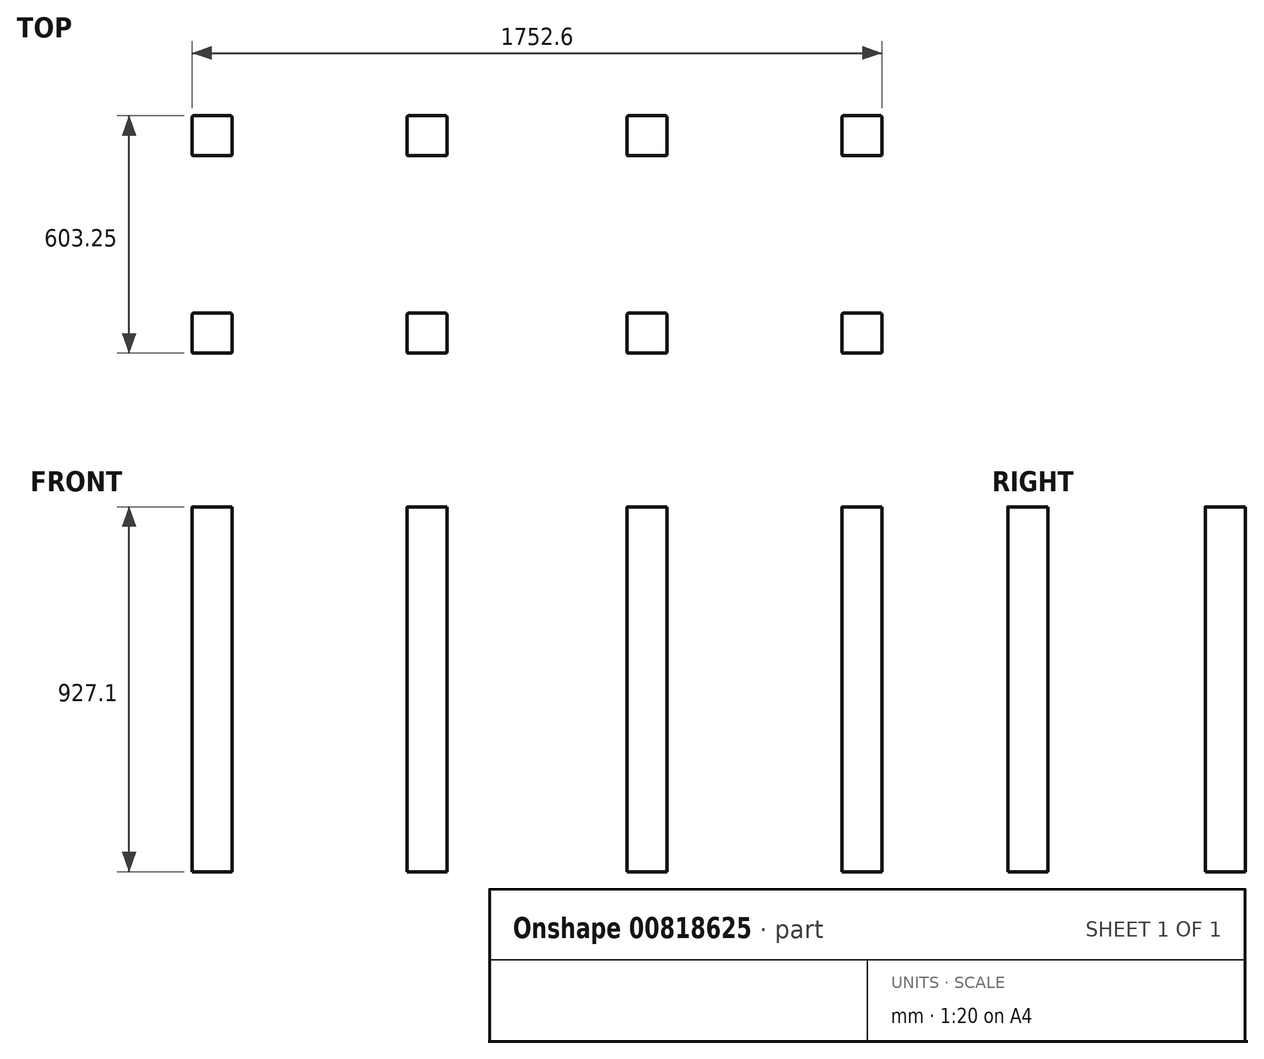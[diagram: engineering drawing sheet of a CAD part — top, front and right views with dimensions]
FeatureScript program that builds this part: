
annotation { "Feature Type Name" : "Feature", "Feature Type Description" : "" }
export const myFeature = defineFeature(function(context is Context, id is Id, definition is map)
    precondition{}
    {
        {
            var Q0;
            Q0=qCreatedBy(makeId("Top.planeOp"),FACE);
            var sketch = newSketch(context, id + "F0", { "sketchPlane" : qUnion([Q0])});
            skPoint(sketch, "E0.middle", {"position": v(0, 0) * mm});
            skLineSegment(sketch, "E1.bottom", {"start": v(-876.3, -285.75) * mm, "end": v(-774.7, -285.75) * mm});
            skLineSegment(sketch, "E1.top", {"start": v(-876.3, -184.15) * mm, "end": v(-774.7, -184.15) * mm});
            skLineSegment(sketch, "E1.left", {"start": v(-876.3, -285.75) * mm, "end": v(-876.3, -184.15) * mm});
            skLineSegment(sketch, "E1.right", {"start": v(-774.7, -285.75) * mm, "end": v(-774.7, -184.15) * mm});
            skLineSegment(sketch, "E2.bottom", {"start": v(-876.3, 317.5) * mm, "end": v(-774.7, 317.5) * mm});
            skLineSegment(sketch, "E2.top", {"start": v(-876.3, 215.9) * mm, "end": v(-774.7, 215.9) * mm});
            skLineSegment(sketch, "E2.left", {"start": v(-876.3, 317.5) * mm, "end": v(-876.3, 215.9) * mm});
            skLineSegment(sketch, "E2.right", {"start": v(-774.7, 317.5) * mm, "end": v(-774.7, 215.9) * mm});
            skLineSegment(sketch, "E3.bottom", {"start": v(876.3, -285.75) * mm, "end": v(774.7, -285.75) * mm});
            skLineSegment(sketch, "E3.top", {"start": v(876.3, -184.15) * mm, "end": v(774.7, -184.15) * mm});
            skLineSegment(sketch, "E3.left", {"start": v(876.3, -285.75) * mm, "end": v(876.3, -184.15) * mm});
            skLineSegment(sketch, "E3.right", {"start": v(774.7, -285.75) * mm, "end": v(774.7, -184.15) * mm});
            skLineSegment(sketch, "E4.bottom", {"start": v(876.3, 317.5) * mm, "end": v(774.7, 317.5) * mm});
            skLineSegment(sketch, "E4.top", {"start": v(876.3, 215.9) * mm, "end": v(774.7, 215.9) * mm});
            skLineSegment(sketch, "E4.left", {"start": v(876.3, 317.5) * mm, "end": v(876.3, 215.9) * mm});
            skLineSegment(sketch, "E4.right", {"start": v(774.7, 317.5) * mm, "end": v(774.7, 215.9) * mm});
            skLineSegment(sketch, "E5.bottom", {"start": v(-330.2, -285.75) * mm, "end": v(-228.6, -285.75) * mm});
            skLineSegment(sketch, "E5.top", {"start": v(-330.2, -184.15) * mm, "end": v(-228.6, -184.15) * mm});
            skLineSegment(sketch, "E5.left", {"start": v(-330.2, -285.75) * mm, "end": v(-330.2, -184.15) * mm});
            skLineSegment(sketch, "E5.right", {"start": v(-228.6, -285.75) * mm, "end": v(-228.6, -184.15) * mm});
            skLineSegment(sketch, "E6.bottom", {"start": v(330.2, -285.75) * mm, "end": v(228.6, -285.75) * mm});
            skLineSegment(sketch, "E6.top", {"start": v(330.2, -184.15) * mm, "end": v(228.6, -184.15) * mm});
            skLineSegment(sketch, "E6.left", {"start": v(330.2, -285.75) * mm, "end": v(330.2, -184.15) * mm});
            skLineSegment(sketch, "E6.right", {"start": v(228.6, -285.75) * mm, "end": v(228.6, -184.15) * mm});
            skLineSegment(sketch, "E7.bottom", {"start": v(330.2, 317.5) * mm, "end": v(228.6, 317.5) * mm});
            skLineSegment(sketch, "E7.top", {"start": v(330.2, 215.9) * mm, "end": v(228.6, 215.9) * mm});
            skLineSegment(sketch, "E7.left", {"start": v(330.2, 317.5) * mm, "end": v(330.2, 215.9) * mm});
            skLineSegment(sketch, "E7.right", {"start": v(228.6, 317.5) * mm, "end": v(228.6, 215.9) * mm});
            skLineSegment(sketch, "E8.bottom", {"start": v(-330.2, 317.5) * mm, "end": v(-228.6, 317.5) * mm});
            skLineSegment(sketch, "E8.top", {"start": v(-330.2, 215.9) * mm, "end": v(-228.6, 215.9) * mm});
            skLineSegment(sketch, "E8.left", {"start": v(-330.2, 317.5) * mm, "end": v(-330.2, 215.9) * mm});
            skLineSegment(sketch, "E8.right", {"start": v(-228.6, 317.5) * mm, "end": v(-228.6, 215.9) * mm});
            skPoint(sketch, "E0.right.end.orphan", {"position": v(-914.4, -323.85) * mm});
            skPoint(sketch, "E0.bottom.end.orphan", {"position": v(-914.4, 323.85) * mm});
            skPoint(sketch, "E0.left.end.orphan", {"position": v(914.4, -323.85) * mm});
            skPoint(sketch, "E0.left.start.orphan", {"position": v(914.4, 323.85) * mm});
            skSolve(sketch);
        }
        {
            var Q0;
            Q0=makeQuery(id+"F0.imprint","IMPRINT",FACE,{"disambiguationData":[TD([[makeQuery(id+"F0.imprint","IMPRINT",EDGE,{"derivedFrom":sQuery(id+"F0.wireOp",EDGE,"E4.bottom")}),1.0]])]});
            var Q1;
            Q1=makeQuery(id+"F0.imprint","IMPRINT",FACE,{"disambiguationData":[TD([[makeQuery(id+"F0.imprint","IMPRINT",EDGE,{"derivedFrom":sQuery(id+"F0.wireOp",EDGE,"E7.bottom")}),1.0]])]});
            var Q2;
            Q2=makeQuery(id+"F0.imprint","IMPRINT",FACE,{"disambiguationData":[TD([[makeQuery(id+"F0.imprint","IMPRINT",EDGE,{"derivedFrom":sQuery(id+"F0.wireOp",EDGE,"E8.bottom")}),-1.0]])]});
            var Q3;
            Q3=makeQuery(id+"F0.imprint","IMPRINT",FACE,{"disambiguationData":[TD([[makeQuery(id+"F0.imprint","IMPRINT",EDGE,{"derivedFrom":sQuery(id+"F0.wireOp",EDGE,"E2.bottom")}),-1.0]])]});
            var Q4;
            Q4=makeQuery(id+"F0.imprint","IMPRINT",FACE,{"disambiguationData":[TD([[makeQuery(id+"F0.imprint","IMPRINT",EDGE,{"derivedFrom":sQuery(id+"F0.wireOp",EDGE,"E1.bottom")}),1.0]])]});
            var Q5;
            Q5=makeQuery(id+"F0.imprint","IMPRINT",FACE,{"disambiguationData":[TD([[makeQuery(id+"F0.imprint","IMPRINT",EDGE,{"derivedFrom":sQuery(id+"F0.wireOp",EDGE,"E3.bottom")}),-1.0]])]});
            var Q6;
            Q6=makeQuery(id+"F0.imprint","IMPRINT",FACE,{"disambiguationData":[TD([[makeQuery(id+"F0.imprint","IMPRINT",EDGE,{"derivedFrom":sQuery(id+"F0.wireOp",EDGE,"E6.bottom")}),-1.0]])]});
            var Q7;
            Q7=makeQuery(id+"F0.imprint","IMPRINT",FACE,{"disambiguationData":[TD([[makeQuery(id+"F0.imprint","IMPRINT",EDGE,{"derivedFrom":sQuery(id+"F0.wireOp",EDGE,"E5.bottom")}),1.0]])]});
            extrude(context, id + "F1", {"entities" : qUnion([Q0, Q1, Q2, Q3, Q4, Q5, Q6, Q7]), "depth" : 927.1 * mm, "offsetDistance" : 25.4 * mm});
        }
        {
            var Q0;
            Q0=makeQuery(id+"F1.opExtrude","SWEPT_EDGE",EDGE,{"disambiguationData":[OSD([sQuery(id+"F0.wireOp",EDGE,"E1.bottom"),sQuery(id+"F0.wireOp",EDGE,"E1.left")])]});
            var Q1;
            Q1=makeQuery(id+"F1.opExtrude","SWEPT_EDGE",EDGE,{"disambiguationData":[OSD([sQuery(id+"F0.wireOp",EDGE,"E1.bottom"),sQuery(id+"F0.wireOp",EDGE,"E1.right")])]});
            var Q2;
            Q2=makeQuery(id+"F1.opExtrude","SWEPT_EDGE",EDGE,{"disambiguationData":[OSD([sQuery(id+"F0.wireOp",EDGE,"E1.top"),sQuery(id+"F0.wireOp",EDGE,"E1.right")])]});
            var Q3;
            Q3=makeQuery(id+"F1.opExtrude","SWEPT_EDGE",EDGE,{"disambiguationData":[OSD([sQuery(id+"F0.wireOp",EDGE,"E2.top"),sQuery(id+"F0.wireOp",EDGE,"E2.left")])]});
            var Q4;
            Q4=makeQuery(id+"F1.opExtrude","SWEPT_EDGE",EDGE,{"disambiguationData":[OSD([sQuery(id+"F0.wireOp",EDGE,"E2.top"),sQuery(id+"F0.wireOp",EDGE,"E2.right")])]});
            var Q5;
            Q5=makeQuery(id+"F1.opExtrude","SWEPT_EDGE",EDGE,{"disambiguationData":[OSD([sQuery(id+"F0.wireOp",EDGE,"E2.bottom"),sQuery(id+"F0.wireOp",EDGE,"E2.right")])]});
            var Q6;
            Q6=makeQuery(id+"F1.opExtrude","SWEPT_EDGE",EDGE,{"disambiguationData":[OSD([sQuery(id+"F0.wireOp",EDGE,"E5.bottom"),sQuery(id+"F0.wireOp",EDGE,"E5.left")])]});
            var Q7;
            Q7=makeQuery(id+"F1.opExtrude","SWEPT_EDGE",EDGE,{"disambiguationData":[OSD([sQuery(id+"F0.wireOp",EDGE,"E5.bottom"),sQuery(id+"F0.wireOp",EDGE,"E5.right")])]});
            var Q8;
            Q8=makeQuery(id+"F1.opExtrude","SWEPT_EDGE",EDGE,{"disambiguationData":[OSD([sQuery(id+"F0.wireOp",EDGE,"E5.top"),sQuery(id+"F0.wireOp",EDGE,"E5.right")])]});
            var Q9;
            Q9=makeQuery(id+"F1.opExtrude","SWEPT_EDGE",EDGE,{"disambiguationData":[OSD([sQuery(id+"F0.wireOp",EDGE,"E8.top"),sQuery(id+"F0.wireOp",EDGE,"E8.left")])]});
            var Q10;
            Q10=makeQuery(id+"F1.opExtrude","SWEPT_EDGE",EDGE,{"disambiguationData":[OSD([sQuery(id+"F0.wireOp",EDGE,"E8.top"),sQuery(id+"F0.wireOp",EDGE,"E8.right")])]});
            var Q11;
            Q11=makeQuery(id+"F1.opExtrude","SWEPT_EDGE",EDGE,{"disambiguationData":[OSD([sQuery(id+"F0.wireOp",EDGE,"E8.bottom"),sQuery(id+"F0.wireOp",EDGE,"E8.right")])]});
            var Q12;
            Q12=makeQuery(id+"F1.opExtrude","SWEPT_EDGE",EDGE,{"disambiguationData":[OSD([sQuery(id+"F0.wireOp",EDGE,"E6.bottom"),sQuery(id+"F0.wireOp",EDGE,"E6.right")])]});
            var Q13;
            Q13=makeQuery(id+"F1.opExtrude","SWEPT_EDGE",EDGE,{"disambiguationData":[OSD([sQuery(id+"F0.wireOp",EDGE,"E6.top"),sQuery(id+"F0.wireOp",EDGE,"E6.left")])]});
            var Q14;
            Q14=makeQuery(id+"F1.opExtrude","SWEPT_EDGE",EDGE,{"disambiguationData":[OSD([sQuery(id+"F0.wireOp",EDGE,"E7.top"),sQuery(id+"F0.wireOp",EDGE,"E7.right")])]});
            var Q15;
            Q15=makeQuery(id+"F1.opExtrude","SWEPT_EDGE",EDGE,{"disambiguationData":[OSD([sQuery(id+"F0.wireOp",EDGE,"E7.top"),sQuery(id+"F0.wireOp",EDGE,"E7.left")])]});
            var Q16;
            Q16=makeQuery(id+"F1.opExtrude","SWEPT_EDGE",EDGE,{"disambiguationData":[OSD([sQuery(id+"F0.wireOp",EDGE,"E7.bottom"),sQuery(id+"F0.wireOp",EDGE,"E7.left")])]});
            var Q17;
            Q17=makeQuery(id+"F1.opExtrude","SWEPT_EDGE",EDGE,{"disambiguationData":[OSD([sQuery(id+"F0.wireOp",EDGE,"E3.bottom"),sQuery(id+"F0.wireOp",EDGE,"E3.left")])]});
            var Q18;
            Q18=makeQuery(id+"F1.opExtrude","SWEPT_EDGE",EDGE,{"disambiguationData":[OSD([sQuery(id+"F0.wireOp",EDGE,"E3.bottom"),sQuery(id+"F0.wireOp",EDGE,"E3.right")])]});
            var Q19;
            Q19=makeQuery(id+"F1.opExtrude","SWEPT_EDGE",EDGE,{"disambiguationData":[OSD([sQuery(id+"F0.wireOp",EDGE,"E3.top"),sQuery(id+"F0.wireOp",EDGE,"E3.left")])]});
            var Q20;
            Q20=makeQuery(id+"F1.opExtrude","SWEPT_EDGE",EDGE,{"disambiguationData":[OSD([sQuery(id+"F0.wireOp",EDGE,"E4.top"),sQuery(id+"F0.wireOp",EDGE,"E4.right")])]});
            var Q21;
            Q21=makeQuery(id+"F1.opExtrude","SWEPT_EDGE",EDGE,{"disambiguationData":[OSD([sQuery(id+"F0.wireOp",EDGE,"E4.bottom"),sQuery(id+"F0.wireOp",EDGE,"E4.left")])]});
            var Q22;
            Q22=makeQuery(id+"F1.opExtrude","SWEPT_EDGE",EDGE,{"disambiguationData":[OSD([sQuery(id+"F0.wireOp",EDGE,"E4.top"),sQuery(id+"F0.wireOp",EDGE,"E4.left")])]});
            var Q23;
            Q23=makeQuery(id+"F1.opExtrude","SWEPT_EDGE",EDGE,{"disambiguationData":[OSD([sQuery(id+"F0.wireOp",EDGE,"E3.top"),sQuery(id+"F0.wireOp",EDGE,"E3.right")])]});
            var Q24;
            Q24=makeQuery(id+"F1.opExtrude","SWEPT_EDGE",EDGE,{"disambiguationData":[OSD([sQuery(id+"F0.wireOp",EDGE,"E6.bottom"),sQuery(id+"F0.wireOp",EDGE,"E6.left")])]});
            var Q25;
            Q25=makeQuery(id+"F1.opExtrude","SWEPT_EDGE",EDGE,{"disambiguationData":[OSD([sQuery(id+"F0.wireOp",EDGE,"E4.bottom"),sQuery(id+"F0.wireOp",EDGE,"E4.right")])]});
            var Q26;
            Q26=makeQuery(id+"F1.opExtrude","SWEPT_EDGE",EDGE,{"disambiguationData":[OSD([sQuery(id+"F0.wireOp",EDGE,"E6.top"),sQuery(id+"F0.wireOp",EDGE,"E6.right")])]});
            var Q27;
            Q27=makeQuery(id+"F1.opExtrude","SWEPT_EDGE",EDGE,{"disambiguationData":[OSD([sQuery(id+"F0.wireOp",EDGE,"E7.bottom"),sQuery(id+"F0.wireOp",EDGE,"E7.right")])]});
            var Q28;
            Q28=makeQuery(id+"F1.opExtrude","SWEPT_EDGE",EDGE,{"disambiguationData":[OSD([sQuery(id+"F0.wireOp",EDGE,"E5.top"),sQuery(id+"F0.wireOp",EDGE,"E5.left")])]});
            var Q29;
            Q29=makeQuery(id+"F1.opExtrude","SWEPT_EDGE",EDGE,{"disambiguationData":[OSD([sQuery(id+"F0.wireOp",EDGE,"E8.bottom"),sQuery(id+"F0.wireOp",EDGE,"E8.left")])]});
            var Q30;
            Q30=makeQuery(id+"F1.opExtrude","SWEPT_EDGE",EDGE,{"disambiguationData":[OSD([sQuery(id+"F0.wireOp",EDGE,"E1.top"),sQuery(id+"F0.wireOp",EDGE,"E1.left")])]});
            var Q31;
            Q31=makeQuery(id+"F1.opExtrude","SWEPT_EDGE",EDGE,{"disambiguationData":[OSD([sQuery(id+"F0.wireOp",EDGE,"E2.bottom"),sQuery(id+"F0.wireOp",EDGE,"E2.left")])]});
            fillet(context, id + "F2", {"entities" : qUnion([Q0, Q1, Q2, Q3, Q4, Q5, Q6, Q7, Q8, Q9, Q10, Q11, Q12, Q13, Q14, Q15, Q16, Q17, Q18, Q19, Q20, Q21, Q22, Q23, Q24, Q25, Q26, Q27, Q28, Q29, Q30, Q31]), "radius" : 3.17 * mm, "allowEdgeOverflow" : false});
        }
    });
